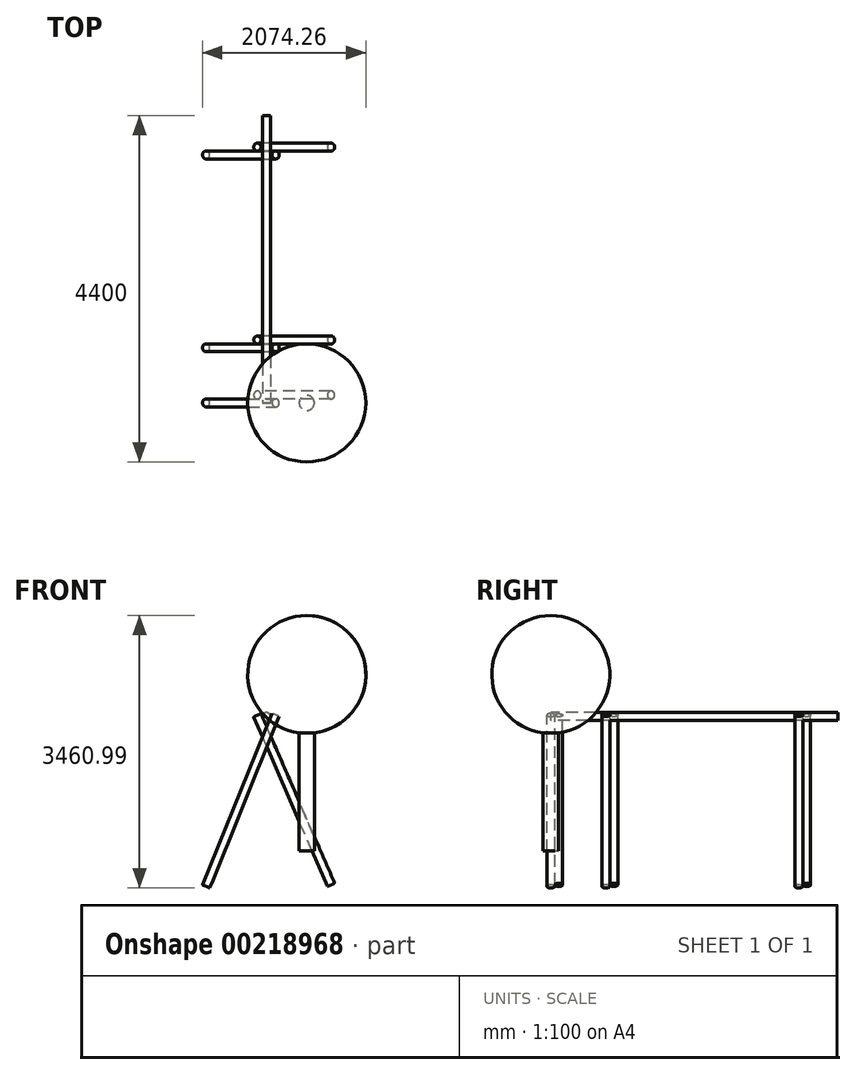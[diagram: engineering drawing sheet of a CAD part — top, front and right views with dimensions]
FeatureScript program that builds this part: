
annotation { "Feature Type Name" : "Feature", "Feature Type Description" : "" }
export const myFeature = defineFeature(function(context is Context, id is Id, definition is map)
    precondition{}
    {
        {
            var Q0;
            Q0=qCreatedBy(makeId("Front.planeOp"),FACE);
            var sketch = newSketch(context, id + "F0", { "sketchPlane" : qUnion([Q0])});
            skLineSegment(sketch, "E0.bottom", {"start": v(0, -803.2) * mm, "end": v(96.43, -803.2) * mm});
            skLineSegment(sketch, "E0.right", {"start": v(96.43, -803.2) * mm, "end": v(96.43, 696.8) * mm});
            skPoint(sketch, "E0.middle", {"position": v(0, -53.2) * mm});
            skArc(sketch, "E1", {"start": v(96.43, 696.8) * mm, "mid": v(748.44, 1488.89) * mm, "end": v(0, 2190.58) * mm});
            skPoint(sketch, "E1.third.point", {"position": v(740.65, 1322.5) * mm});
            skLineSegment(sketch, "E2", {"start": v(0, 2627.26) * mm, "end": v(0, -1534.12) * mm, "construction": true});
            skPoint(sketch, "E3.orphan", {"position": v(-96.43, 696.8) * mm});
            skPoint(sketch, "E4.orphan", {"position": v(-96.43, -803.2) * mm});
            skLineSegment(sketch, "E5", {"start": v(0, 2190.58) * mm, "end": v(0, -803.2) * mm});
            skSolve(sketch);
        }
        {
            var Q0;
            Q0=makeQuery(id+"F0.imprint","IMPRINT",FACE,{"disambiguationData":[TD([[makeQuery(id+"F0.imprint","IMPRINT",EDGE,{"derivedFrom":sQuery(id+"F0.wireOp",EDGE,"E0.bottom")}),1.0]])]});
            var Q1;
            Q1=sQuery(id+"F0.wireOp",EDGE,"E2");
            revolve(context, id + "F1", {"entities" : qUnion([Q0]), "axis" : qUnion([Q1]), "revolveType" : RevolveType.FULL});
        }
        {
            var Q0;
            Q0=qCreatedBy(makeId("Front.planeOp"),FACE);
            var sketch = newSketch(context, id + "F2", { "sketchPlane" : qUnion([Q0])});
            skLineSegment(sketch, "E6.bottom", {"start": v(-441.87, 945.2) * mm, "end": v(-395.53, 926.42) * mm});
            skLineSegment(sketch, "E6.top", {"start": v(-1324.26, -1232.86) * mm, "end": v(-1277.91, -1251.63) * mm});
            skLineSegment(sketch, "E6.left", {"start": v(-441.87, 945.2) * mm, "end": v(-1324.26, -1232.86) * mm});
            skLineSegment(sketch, "E6.right", {"start": v(-395.53, 926.42) * mm, "end": v(-1277.91, -1251.63) * mm});
            skPoint(sketch, "E7", {"position": v(-508.17, 648.37) * mm});
            skLineSegment(sketch, "E8.bottom", {"start": v(-673.62, 903.57) * mm, "end": v(-627.77, 923.5) * mm});
            skLineSegment(sketch, "E8.top", {"start": v(263.19, -1251.63) * mm, "end": v(309.04, -1231.7) * mm});
            skLineSegment(sketch, "E8.left", {"start": v(-673.62, 903.57) * mm, "end": v(263.19, -1251.63) * mm});
            skLineSegment(sketch, "E8.right", {"start": v(-627.77, 923.5) * mm, "end": v(309.04, -1231.7) * mm});
            skLineSegment(sketch, "E9", {"start": v(-651.94, 1104.54) * mm, "end": v(-152.98, -43.36) * mm, "construction": true});
            skCircle(sketch, "E10", {"center": v(-511.42, 906.68) * mm, "radius": 50 * mm});
            skSolve(sketch);
        }
        {
            var Q0;
            {var subQ0=sQuery(id+"F2.wireOp",EDGE,"E6.bottom");Q0=makeQuery(id+"F2.imprint","IMPRINT",FACE,{"disambiguationData":[TD([[makeQuery(id+"F2.imprint","IMPRINT",EDGE,{"derivedFrom":subQ0}),-1.0]])]});}
            var Q1;
            {var subQ0=sQuery(id+"F2.wireOp",EDGE,"E6.top");Q1=makeQuery(id+"F2.imprint","IMPRINT",FACE,{"disambiguationData":[TD([[makeQuery(id+"F2.imprint","IMPRINT",EDGE,{"derivedFrom":subQ0}),1.0]])]});}
            var Q2;
            {var subQ0=sQuery(id+"F2.wireOp",EDGE,"E8.right");var subQ1=sQuery(id+"F2.wireOp",EDGE,"E6.left");var subQ2=makeQuery(id+"F2.imprint","INTERSECT",VERTEX,{"derivedFrom":[subQ1,subQ0]});Q2=makeQuery(id+"F2.imprint","IMPRINT",FACE,{"disambiguationData":[TD([[makeQuery(id+"F2.imprint","IMPRINT",EDGE,{"disambiguationData":[TD([[subQ2,-1.0]])],"derivedFrom":subQ1}),1.0]])]});}
            var Q3;
            Q3=sQuery(id+"F2.wireOp",EDGE,"E6.right");
            revolve(context, id + "F3", {"entities" : qUnion([Q0, Q1, Q2]), "axis" : qUnion([Q3]), "revolveType" : RevolveType.FULL});
        }
        {
            var Q0;
            {var subQ5=sQuery(id+"F2.wireOp",EDGE,"E8.bottom");Q0=makeQuery(id+"F2.imprint","IMPRINT",FACE,{"disambiguationData":[TD([[makeQuery(id+"F2.imprint","IMPRINT",EDGE,{"derivedFrom":subQ5}),-1.0]])]});}
            var Q1;
            {var subQ5=sQuery(id+"F2.wireOp",EDGE,"E8.top");Q1=makeQuery(id+"F2.imprint","IMPRINT",FACE,{"disambiguationData":[TD([[makeQuery(id+"F2.imprint","IMPRINT",EDGE,{"derivedFrom":subQ5}),1.0]])]});}
            var Q2;
            {var subQ0=sQuery(id+"F2.wireOp",EDGE,"E8.right");var subQ1=sQuery(id+"F2.wireOp",EDGE,"E6.left");var subQ2=makeQuery(id+"F2.imprint","INTERSECT",VERTEX,{"derivedFrom":[subQ1,subQ0]});Q2=makeQuery(id+"F2.imprint","IMPRINT",FACE,{"disambiguationData":[TD([[makeQuery(id+"F2.imprint","IMPRINT",EDGE,{"disambiguationData":[TD([[subQ2,-1.0]])],"derivedFrom":subQ1}),1.0]])]});}
            var Q3;
            Q3=sQuery(id+"F2.wireOp",EDGE,"E8.right");
            revolve(context, id + "F4", {"entities" : qUnion([Q0, Q1, Q2]), "axis" : qUnion([Q3]), "revolveType" : RevolveType.FULL});
        }
        {
            var Q0;
            Q0=makeQuery(id+"F4.opRevolve","SWEPT_BODY",BODY,{"disambiguationData":[OSD([sQuery(id+"F2.wireOp",EDGE,"E8.bottom"),sQuery(id+"F2.wireOp",EDGE,"E8.top"),sQuery(id+"F2.wireOp",EDGE,"E8.left"),sQuery(id+"F2.wireOp",EDGE,"E8.right")])]});
            transform(context, id + "F5", {"entities" : qUnion([Q0]), "transformType" : TransformType.TRANSLATION_3D, "dx" : 0 * mm, "dy" : 100 * mm, "dz" : 0 * mm, "makeCopy" : false});
        }
        {
            var Q0;
            Q0=makeQuery(id+"F3.opRevolve","SWEPT_BODY",BODY,{"disambiguationData":[OSD([sQuery(id+"F2.wireOp",EDGE,"E6.bottom"),sQuery(id+"F2.wireOp",EDGE,"E6.top"),sQuery(id+"F2.wireOp",EDGE,"E6.left"),sQuery(id+"F2.wireOp",EDGE,"E6.right")])]});
            var Q1;
            Q1=makeQuery(id+"F4.opRevolve","SWEPT_BODY",BODY,{"disambiguationData":[OSD([sQuery(id+"F2.wireOp",EDGE,"E8.bottom"),sQuery(id+"F2.wireOp",EDGE,"E8.top"),sQuery(id+"F2.wireOp",EDGE,"E8.left"),sQuery(id+"F2.wireOp",EDGE,"E8.right")])]});
            transform(context, id + "F6", {"entities" : qUnion([Q0, Q1]), "transformType" : TransformType.TRANSLATION_3D, "dx" : 0 * mm, "dy" : 700 * mm, "dz" : 0 * mm, "makeCopy" : true});
        }
        {
            var Q0;
            Q0=makeQuery(id+"F3.opRevolve","SWEPT_BODY",BODY,{"disambiguationData":[OSD([sQuery(id+"F2.wireOp",EDGE,"E6.bottom"),sQuery(id+"F2.wireOp",EDGE,"E6.top"),sQuery(id+"F2.wireOp",EDGE,"E6.left"),sQuery(id+"F2.wireOp",EDGE,"E6.right")])]});
            var Q1;
            Q1=makeQuery(id+"F4.opRevolve","SWEPT_BODY",BODY,{"disambiguationData":[OSD([sQuery(id+"F2.wireOp",EDGE,"E8.bottom"),sQuery(id+"F2.wireOp",EDGE,"E8.top"),sQuery(id+"F2.wireOp",EDGE,"E8.left"),sQuery(id+"F2.wireOp",EDGE,"E8.right")])]});
            transform(context, id + "F7", {"entities" : qUnion([Q0, Q1]), "transformType" : TransformType.TRANSLATION_3D, "dx" : 0 * mm, "dy" : 3150 * mm, "dz" : 0 * mm, "makeCopy" : true});
        }
        {
            var Q0;
            Q0=makeQuery(id+"F2.imprint","IMPRINT",FACE,{"disambiguationData":[TD([[makeQuery(id+"F2.imprint","IMPRINT",EDGE,{"derivedFrom":sQuery(id+"F2.wireOp",EDGE,"E10")}),1.0]])]});
            extrude(context, id + "F8", {"entities" : qUnion([Q0]), "oppositeDirection" : true, "depth" : 3650 * mm});
        }
    });
